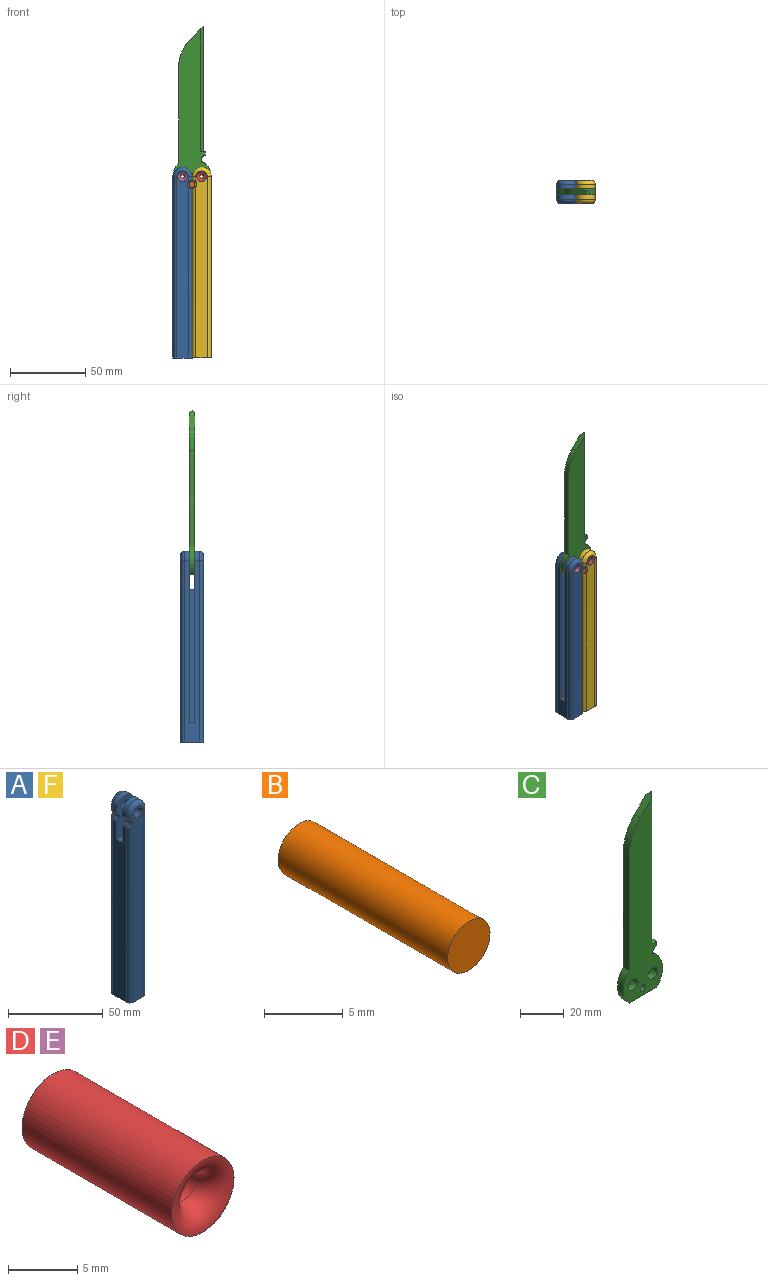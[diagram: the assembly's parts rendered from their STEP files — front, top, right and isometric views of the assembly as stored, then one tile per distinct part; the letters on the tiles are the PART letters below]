
ASSEMBLY  parts=6 mates=5
PART A: 36 faces, bbox 13.7x15.6x127.5 mm
  f0: cylinder r=2.54mm len=3.18mm, axis (0,0,1), area 9.8mm2, adj f3,f8,f20,f34
  f1: cylinder r=2.54mm len=113.67mm, axis (0,0,-1), area 450.7mm2, adj f4,f6,f9,f27
  f2: plane 3.18x2.17mm, normal (-1,0,0), area 6.9mm2, adj f11,f14,f18,f30
  f3: plane 3.18x2.17mm, normal (-1,0,0), area 6.9mm2, adj f0,f12,f15,f35
  f4: plane 112.66x10.16mm, normal (-1,0,0), area 1102.5mm2, adj f1,f6,f11,f12,f13,f21,f26,f31
  f5: cylinder r=3.17mm len=6.35mm, axis (0,-1,0), area 114mm2, adj f9,f11
  f6: plane 15.24x12.7mm, normal (0,0,-1), area 188mm2, adj f1,f4,f7,f8,f9,f16,f19,f21
  f7: plane 120.65x10.16mm, normal (1,0,0), area 814.5mm2, adj f6,f11,f12,f14,f15,f16,f19,f23
  f8: plane 124.46x7.62mm, normal (0,-1,0), area 908.8mm2, adj f0,f6,f10,f19,f20,f21,f33
  f9: plane 124.46x7.62mm, normal (0,1,0), area 908.8mm2, adj f1,f5,f6,f16,f17,f18,f28
  f10: cylinder r=3.17mm len=6.35mm, axis (0,-1,0), area 114mm2, adj f8,f12
  f11: plane 114.3x12.7mm, normal (0,-1,0), area 1086.1mm2, adj f2,f4,f5,f7,f13,f14,f22,f23
  f12: plane 114.3x12.7mm, normal (0,1,0), area 1086.1mm2, adj f3,f4,f7,f10,f13,f15,f22,f23
  f13: plane 3.81x3.49mm, normal (0,0,1), area 13.3mm2, adj f4,f11,f12,f22
  f14: cylinder r=6.35mm len=12.7mm, axis (0,-1,0), area 63.3mm2, adj f2,f7,f11,f17
  f15: cylinder r=6.35mm len=12.7mm, axis (0,1,0), area 63.3mm2, adj f3,f7,f12,f20
  f16: cylinder r=2.54mm len=120.65mm, axis (0,0,1), area 481.4mm2, adj f6,f7,f9,f17
  f17: torus R=3.81mm, axis (0,-1,0), area 68mm2, adj f9,f14,f16,f18
  f18: cylinder r=2.54mm len=3.18mm, axis (0,0,-1), area 9.8mm2, adj f2,f9,f17,f29
  f19: cylinder r=2.54mm len=120.65mm, axis (0,0,-1), area 481.4mm2, adj f6,f7,f8,f20
  f20: torus R=3.81mm, axis (0,-1,0), area 68mm2, adj f0,f8,f15,f19
  f21: cylinder r=2.54mm len=113.67mm, axis (0,0,1), area 450.7mm2, adj f4,f6,f8,f32
  f22: plane 88.9x3.81mm, normal (1,0,0), area 338.7mm2, adj f11,f12,f13,f23
  f23: plane 9.21x3.81mm, normal (0,0,1), area 35.1mm2, adj f7,f11,f12,f22
  f24: cylinder r=1.91mm len=4.45mm, axis (0,1,0), area 19.2mm2, adj f12,f31,f32,f33,f34,f35
  f25: cylinder r=1.91mm len=4.45mm, axis (0,1,0), area 19.2mm2, adj f11,f26,f27,f28,f29,f30
  f26: cylinder r=1.27mm len=3.18mm, axis (0,1,0), area 4.7mm2, adj f4,f11,f25,f27
  f27: bspline ~3.21x3.03mm, area 4.8mm2, adj f1,f25,f26,f28
  f28: torus R=3.17mm, axis (0,-1,0), area 6.1mm2, adj f9,f25,f27,f29
  f29: bspline ~2.76x2.75mm, area 4.8mm2, adj f18,f25,f28,f30
  f30: cylinder r=1.27mm len=3.18mm, axis (0,1,0), area 4.7mm2, adj f2,f11,f25,f29
  f31: cylinder r=1.27mm len=3.18mm, axis (0,1,0), area 4.7mm2, adj f4,f12,f24,f32
  f32: bspline ~3.14x2.76mm, area 4.8mm2, adj f21,f24,f31,f33
  f33: torus R=3.17mm, axis (0,-1,0), area 6.1mm2, adj f8,f24,f32,f34
  f34: bspline ~3.21x3.03mm, area 4.8mm2, adj f0,f24,f33,f35
  f35: cylinder r=1.27mm len=3.18mm, axis (0,1,0), area 4.7mm2, adj f3,f12,f24,f34
PART B: 3 faces, bbox 3.8x15.2x3.8 mm
  f0: cylinder r=1.91mm len=15.24mm, axis (0,1,0), area 182.4mm2, adj f1,f2
  f1: plane 3.81x3.81mm, normal (0,-1,0), area 11.4mm2, adj f0
  f2: plane 3.81x3.81mm, normal (0,1,0), area 11.4mm2, adj f0
PART C: 16 faces, bbox 25.4x3.8x109.4 mm
  f0: plane 107.43x25.4mm, normal (0,-1,0), area 1539.1mm2, adj f1,f3,f4,f5,f6,f7,f8,f9
  f1: plane 9.44x9.25mm, normal (-0.71,0,0.7), area 45.2mm2, adj f0,f2,f11,f14,f15
  f2: plane 107.43x25.4mm, normal (0,1,0), area 1539.1mm2, adj f1,f3,f4,f5,f6,f7,f8,f9
  f3: plane 3.81x2.54mm, normal (1,0,0), area 9.7mm2, adj f0,f2,f12,f13
  f4: plane 64.02x3.81mm, normal (-1,0,0), area 243.9mm2, adj f0,f2,f6,f11
  f5: cylinder r=12.7mm len=18.14mm, axis (0,-1,0), area 77mm2, adj f0,f2,f7,f12
  f6: cylinder r=12.7mm len=18.14mm, axis (0,-1,0), area 77mm2, adj f0,f2,f4,f7
  f7: plane 17.78x3.81mm, normal (0,0,-1), area 67.7mm2, adj f0,f2,f5,f6
  f8: cylinder r=3.17mm len=6.35mm, axis (0,-1,0), area 76mm2, adj f0,f2
  f9: cylinder r=3.17mm len=6.35mm, axis (0,-1,0), area 76mm2, adj f0,f2
  f10: cylinder r=1.91mm len=3.81mm, axis (0,-1,0), area 45.6mm2, adj f0,f2
  f11: cylinder r=25.4mm len=17.78mm, axis (0,-1,0), area 75mm2, adj f0,f1,f2,f4
  f12: cylinder r=2.54mm len=5.08mm, axis (0,-1,0), area 30.4mm2, adj f0,f2,f3,f5
  f13: plane 3.81x3.18mm, normal (0,0,1), area 8.5mm2, adj f0,f2,f3,f14,f15
  f14: plane 83.61x1.91mm, normal (0.71,-0.71,0), area 222.6mm2, adj f0,f1,f13,f15
  f15: plane 83.61x1.91mm, normal (0.71,0.71,0), area 222.6mm2, adj f1,f2,f13,f14
PART D: 4 faces, bbox 9.8x15.2x9.8 mm
  f0: cylinder r=3.17mm len=15.24mm, axis (0,1,0), area 304mm2, adj f2,f3
  f1: cylinder r=1.27mm len=11.43mm, axis (0,-1,0), area 91.2mm2, adj f2,f3
  f2: torus R=3.17mm, axis (0,-1,0), area 36.9mm2, adj f0,f1
  f3: torus R=3.17mm, axis (0,-1,0), area 36.9mm2, adj f0,f1
PART E: same geometry as D
PART F: same geometry as A
PLACE A rot(axis=(0,0,1),180deg) t=(-28.62,8.09,-127.66)mm
PLACE B t=(-28.62,23.33,-12.09)mm
PLACE C t=(-37.51,17.62,-7.01)mm fixed
PLACE D t=(-22.27,23.33,-7.01)mm
PLACE E t=(-34.97,23.33,-7.01)mm
PLACE F rot(axis=(0,-1,0),0deg) t=(-28.62,23.33,-127.66)mm
MATE fastened B.f0 <-> C.f10  axis (0,1,0) through (-28.62,15.71,-12.09)mm
MATE revolute A.f5 <-> E.f0  axis (0,-1,0) through (-34.97,8.09,-7.01)mm
MATE fastened D.f0 <-> C.f8  axis (0,1,0) through (-22.27,15.71,-7.01)mm
MATE fastened E.f0 <-> C.f9  axis (0,1,0) through (-34.97,15.71,-7.01)mm
MATE revolute F.f5 <-> D.f0  axis (0,-1,0) through (-22.27,8.09,-7.01)mm
